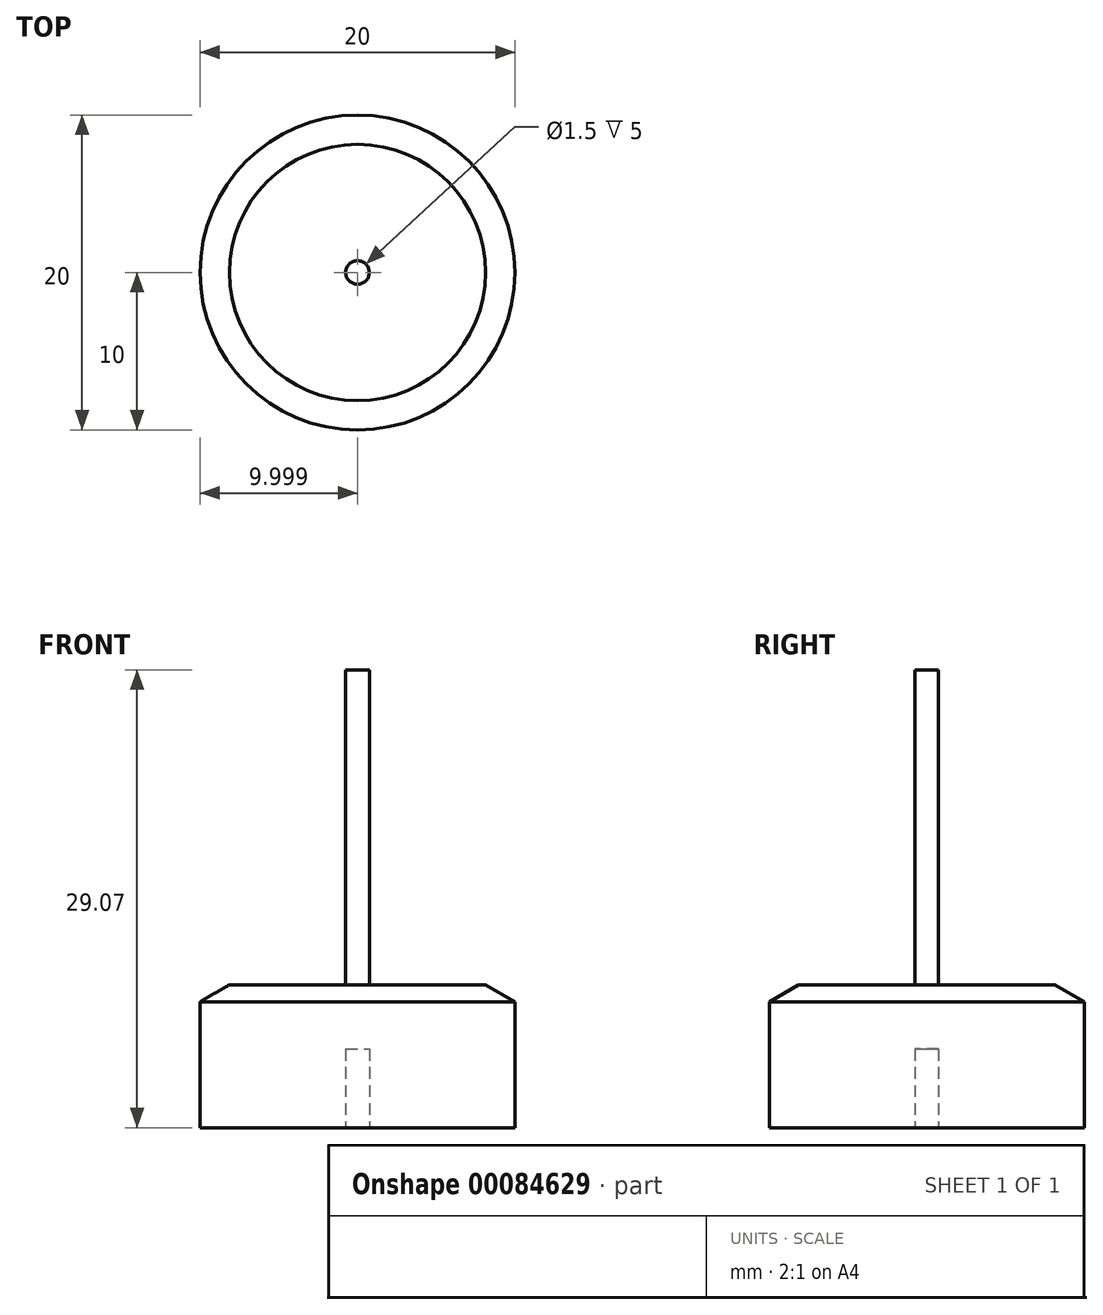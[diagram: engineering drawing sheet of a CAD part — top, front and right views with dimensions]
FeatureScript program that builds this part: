
annotation { "Feature Type Name" : "Feature", "Feature Type Description" : "" }
export const myFeature = defineFeature(function(context is Context, id is Id, definition is map)
    precondition{}
    {
        {
            var Q0;
            Q0=qCreatedBy(makeId("Front.planeOp"),FACE);
            var sketch = newSketch(context, id + "F0", { "sketchPlane" : qUnion([Q0])});
            skLineSegment(sketch, "E0.bottom", {"start": v(-30.55, 8) * mm, "end": v(-20.55, 8) * mm});
            skLineSegment(sketch, "E0.top", {"start": v(-30.55, 0) * mm, "end": v(-21.3, 0) * mm});
            skLineSegment(sketch, "E0.left", {"start": v(-30.55, 8) * mm, "end": v(-30.55, 0) * mm});
            skPoint(sketch, "E1", {"position": v(-20.55, 8) * mm});
            skPoint(sketch, "E2", {"position": v(-20.55, 0) * mm});
            skPoint(sketch, "E3", {"position": v(-20.55, 9.07) * mm});
            skLineSegment(sketch, "E4", {"start": v(-20.55, 8) * mm, "end": v(-20.55, 9.07) * mm});
            skLineSegment(sketch, "E5", {"start": v(-30.55, 8) * mm, "end": v(-28.7, 9.07) * mm});
            skLineSegment(sketch, "E6", {"start": v(-28.7, 9.07) * mm, "end": v(-20.55, 9.07) * mm});
            skLineSegment(sketch, "E7", {"start": v(-20.55, 8) * mm, "end": v(-20.55, 5) * mm});
            skPoint(sketch, "E0.right.end.orphan", {"position": v(-10.55, 0) * mm});
            skPoint(sketch, "E8.start.orphan", {"position": v(-10.55, 8) * mm});
            skLineSegment(sketch, "E9", {"start": v(-20.55, 9.07) * mm, "end": v(-20.55, 29.07) * mm});
            skLineSegment(sketch, "E10", {"start": v(-20.55, 29.07) * mm, "end": v(-21.3, 29.07) * mm});
            skLineSegment(sketch, "E11", {"start": v(-21.3, 29.07) * mm, "end": v(-21.3, 0) * mm});
            skPoint(sketch, "E12.start.orphan", {"position": v(-20.55, 4) * mm});
            skLineSegment(sketch, "E13", {"start": v(-20.55, 5) * mm, "end": v(-21.3, 5) * mm});
            skPoint(sketch, "E14", {"position": v(-20.55, 5) * mm});
            skSolve(sketch);
        }
        {
            var Q0;
            {var subQ0=sQuery(id+"F0.wireOp",EDGE,"E9");Q0=makeQuery(id+"F0.imprint","IMPRINT",FACE,{"disambiguationData":[TD([[makeQuery(id+"F0.imprint","IMPRINT",EDGE,{"derivedFrom":subQ0}),1.0]])]});}
            var Q1;
            {var subQ5=sQuery(id+"F0.wireOp",EDGE,"E0.top");Q1=makeQuery(id+"F0.imprint","IMPRINT",FACE,{"disambiguationData":[TD([[makeQuery(id+"F0.imprint","IMPRINT",EDGE,{"derivedFrom":subQ5}),1.0]])]});}
            var Q2;
            {var subQ0=sQuery(id+"F0.wireOp",EDGE,"E5");Q2=makeQuery(id+"F0.imprint","IMPRINT",FACE,{"disambiguationData":[TD([[makeQuery(id+"F0.imprint","IMPRINT",EDGE,{"derivedFrom":subQ0}),-1.0]])]});}
            var Q3;
            {var subQ0=sQuery(id+"F0.wireOp",EDGE,"E7");Q3=makeQuery(id+"F0.imprint","IMPRINT",FACE,{"disambiguationData":[TD([[makeQuery(id+"F0.imprint","IMPRINT",EDGE,{"derivedFrom":subQ0}),-1.0]])]});}
            var Q4;
            {var subQ0=sQuery(id+"F0.wireOp",EDGE,"E4");Q4=makeQuery(id+"F0.imprint","IMPRINT",FACE,{"disambiguationData":[TD([[makeQuery(id+"F0.imprint","IMPRINT",EDGE,{"derivedFrom":subQ0}),1.0]])]});}
            var Q5;
            Q5=sQuery(id+"F0.wireOp",EDGE,"E9");
            revolve(context, id + "F1", {"entities" : qUnion([Q0, Q1, Q2, Q3, Q4]), "axis" : qUnion([Q5]), "revolveType" : RevolveType.FULL});
        }
    });
